# Revit family: Hager-Univers-IP43-D349-H598-Cl.II-Fire_res.encl_30min-PL-pl
name_source: partatom
category: Equipement électrique
units: mm (PartAtom-declared; Revit-internal decimal feet)

## family parameters
Configuration du panneau = Deux colonnes, circuits au sein
Cote de connecteur circulaire = Utiliser le diamètre
Couper avec des vides une fois chargée = Non
Hôte = Face
Partagée = Non
Point de calcul de pièce = Non
Type d'élément = Tableau de raccordement

## types (2) — shared parameters
Commentaires du type = Univers
EF000003 - Sposób montażu = EV000384 - Montaż natynkowy
EF000007 - Kolor = EV000270 - Szary
EF000040 - Wysokość = 598 mm  [stored 1.96194 ft]
EF000049 - Głębokość = 349 mm  [stored 1.14501 ft]
EF000116 - Numer RAL = 7035
EF000118 - Z płytą montażową = Non
EF000266 - Liczba rzędów = 3
EF000339 - Rodzaj pokrywy = EV004216 - Drzwi
EF001088 - Możliwość rozbudowy = Non
EF001131 - Głębokość wewnętrzna = 240 mm
EF001596 - Materiał obudowy = EV000139 - Tworzywo sztuczne
EF001613 - Podtrzymanie funkcji = EV004178 - E 30
EF003532 - Do zastosowań zewnętrznych = Non
EF004293 - Odporność udarowa = EV008784 - IK10
EF004464 - Rodzaj drzwi = EV002646 - Pojedynczy
EF006244 - Transparentna pokrywa/drzwi = Non
EF006306 - Z zamkiem = Oui
EF007800 - Do ochrony odgromowej = Non
EF008873 - Prąd znamionowy (In) = 250 A
EF009170 - Obudowa z materiału o wysokiej wytrzymałości mechanicznej = 70 mm  [stored 0.229659 ft]
EF009171 - Drzwi/pokrywa z materiału o wysokiej wytrzymałości mechanicznej = 22 mm  [stored 0.0721785 ft]
EF009212 - Wykonanie pokrywy = EV000116 - Zamknięty
EF015940 - Pokrywa z wyzwalaczem nadciśnieniowym = Non
Fabricant = Hager
HG000002 - Z drzwiami lub pokrywą = Oui
HG000003 - Zakres = Univers
HG000006 - Montaż podtynkowy = Non
HG000009 - Drzwi dwuskrzydłowe = Non
HG000010 - Drzwi asymetryczne = Non
HG000023 - Obudowa dwusekcyjna = Non
HG000024 - Wysokość części dolnej = 800 mm
HG000026 - Stojąca = Non
zero-valued in all types: EF000218 - Głębokość wbudowania, Elévation par défaut, HG000027 - Wysokość cokołu

## per-type parameters (varying)
| type | EF000008 - Szerokość | EF000437 - Liczba wejść kablowych | EF002950 - Szerokość wyrażona liczbą modułów | EF004427 - Liczba modułów | EF005474 - Stopień ochrony (IP) | EF009554 - Liczba otworów pod flansze | HG000004 - Referencja producenta |
| Montaż natynkowy IP43 S648 W598 G349  - FB32LE | 648 mm | 2 | 24 | 72 | EV006610 - IP43 | 4 | FB32LE |
| Montaż natynkowy IP44 S398 W598 G349  - FB31LE | 398 mm  [stored 1.30577 ft] | 1 | 12 | 36 | EV006418 - IP44 | 2 | FB31LE |

note: [stored X ft] marks values corroborated as IEEE doubles in the binary element streams (Revit-internal decimal feet)

## geometry (parser evidence)
native form markers: Sweep x10
no freeform markers — native parametric forms only
